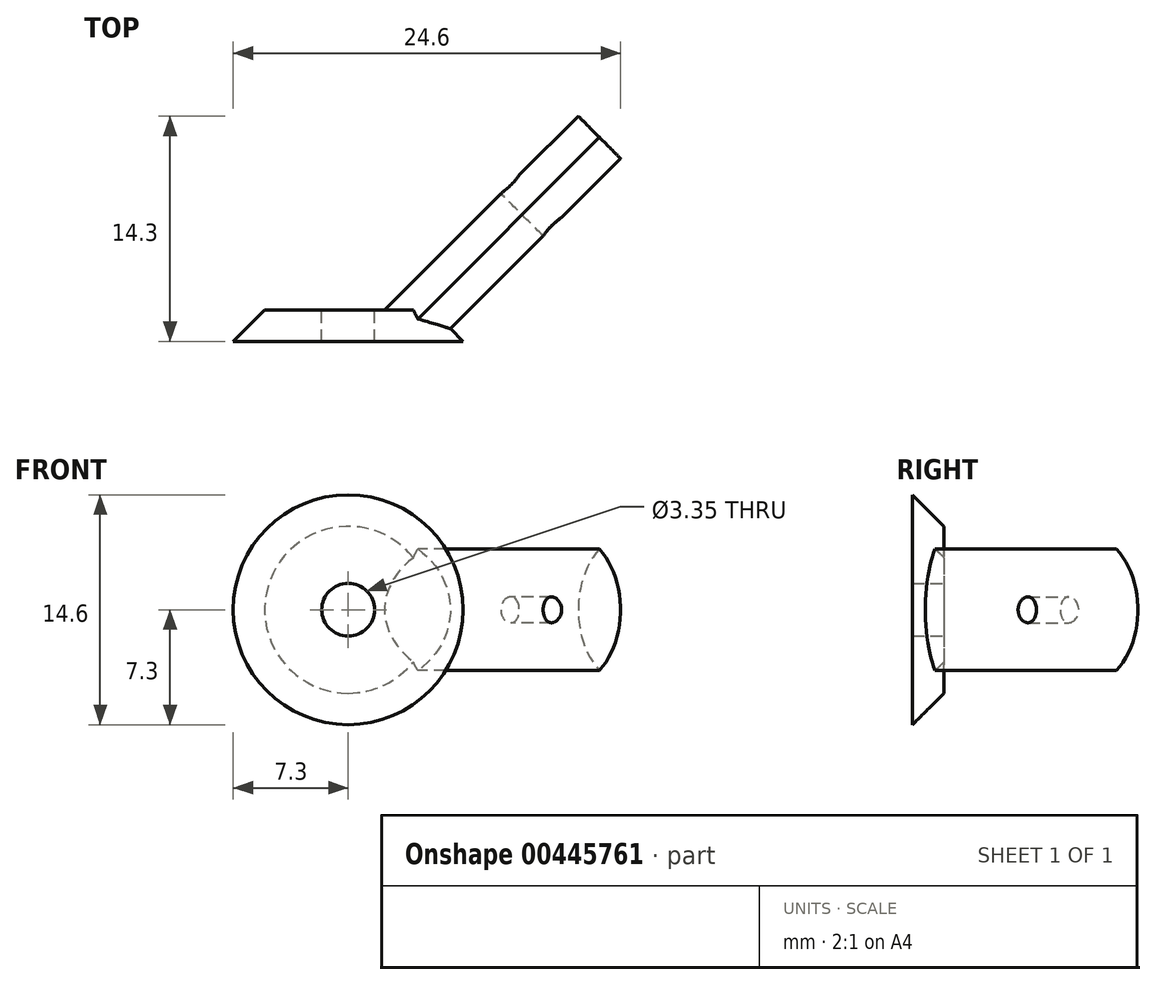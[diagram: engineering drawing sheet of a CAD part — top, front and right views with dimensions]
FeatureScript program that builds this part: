
annotation { "Feature Type Name" : "Feature", "Feature Type Description" : "" }
export const myFeature = defineFeature(function(context is Context, id is Id, definition is map)
    precondition{}
    {
        {
            var Q0;
            Q0=qCreatedBy(makeId("Front.planeOp"),FACE);
            var sketch = newSketch(context, id + "F0", { "sketchPlane" : qUnion([Q0])});
            skCircle(sketch, "E0", {"center": v(0, 0) * mm, "radius": 8.3 * mm});
            skSolve(sketch);
        }
        {
            var Q0;
            Q0=makeQuery(id+"F0.imprint","IMPRINT",FACE,{"disambiguationData":[TD([[makeQuery(id+"F0.imprint","IMPRINT",EDGE,{"derivedFrom":sQuery(id+"F0.wireOp",EDGE,"E0")}),1.0]])]});
            extrude(context, id + "F1", {"entities" : qUnion([Q0]), "depth" : 2 * mm});
        }
        {
            var Q0;
            Q0=makeQuery(id+"F1.opExtrude","CAP_FACE",FACE,{"disambiguationData":[OSD([sQuery(id+"F0.wireOp",EDGE,"E0")])],"isStart":true});
            var sketch = newSketch(context, id + "F2", { "sketchPlane" : qUnion([Q0])});
            skCircle(sketch, "E1", {"center": v(0, 0) * mm, "radius": 1.67 * mm});
            skSolve(sketch);
        }
        {
            var Q0;
            Q0=makeQuery(id+"F2.imprint","IMPRINT",FACE,{"disambiguationData":[TD([[makeQuery(id+"F2.imprint","IMPRINT",EDGE,{"derivedFrom":sQuery(id+"F2.wireOp",EDGE,"E1")}),1.0]])]});
            extrude(context, id + "F3", {"entities" : qUnion([Q0]), "operationType" : NewBodyOperationType.REMOVE, "oppositeDirection" : true, "depth" : 25 * mm});
        }
        {
            var Q0;
            Q0=qCreatedBy(makeId("Right.planeOp"),FACE);
            cPlane(context, id + "F4", {"entities" : qUnion([Q0]), "cplaneType" : CPlaneType.OFFSET, "offset" : 5 * mm, "width" : 150 * mm, "height" : 150 * mm});
        }
        {
            var Q0;
            Q0=qCreatedBy(id+"F4.planeOp",FACE);
            var sketch = newSketch(context, id + "F5", { "sketchPlane" : qUnion([Q0])});
            skLineSegment(sketch, "E2", {"start": v(0, 0) * mm, "end": v(0, 8.61) * mm, "construction": true});
            skSolve(sketch);
        }
        {
            var Q0;
            Q0=qCreatedBy(id+"F4.planeOp",FACE);
            var Q1;
            Q1=sQuery(id+"F5.wireOp",EDGE,"E2");
            cPlane(context, id + "F6", {"entities" : qUnion([Q0, Q1]), "cplaneType" : CPlaneType.LINE_ANGLE, "offset" : 0 * mm, "angle" : 45 * degree, "width" : 150 * mm, "height" : 150 * mm});
        }
        {
            var Q0;
            Q0=qCreatedBy(id+"F6.planeOp",FACE);
            var sketch = newSketch(context, id + "F7", { "sketchPlane" : qUnion([Q0])});
            skLineSegment(sketch, "E3", {"start": v(3.54, 3.85) * mm, "end": v(3.54, -3.85) * mm, "construction": true});
            skLineSegment(sketch, "E4", {"start": v(1.64, 0) * mm, "end": v(5.44, 0) * mm, "construction": true});
            skPoint(sketch, "E4.endSnap0", {"position": v(3.54, 0) * mm});
            skArc(sketch, "E5", {"start": v(3.54, -3.85) * mm, "mid": v(5.44, 0) * mm, "end": v(3.54, 3.85) * mm});
            skArc(sketch, "E6", {"start": v(3.54, 3.85) * mm, "mid": v(1.64, 0) * mm, "end": v(3.54, -3.85) * mm});
            skSolve(sketch);
        }
        {
            var Q0;
            Q0=makeQuery(id+"F7.imprint","IMPRINT",FACE,{"disambiguationData":[TD([[makeQuery(id+"F7.imprint","IMPRINT",EDGE,{"derivedFrom":sQuery(id+"F7.wireOp",EDGE,"E5")}),1.0]])]});
            var Q1;
            Q1=sQuery(id+"F7.wireOp",EDGE,"E6");
            var Q2;
            Q2=sQuery(id+"F7.wireOp",EDGE,"E5");
            var Q3;
            Q3=makeQuery(id+"F1.opExtrude","CAP_FACE",FACE,{"disambiguationData":[OSD([sQuery(id+"F0.wireOp",EDGE,"E0")])],"isStart":true});
            extrude(context, id + "F8", {"entities" : qUnion([Q0]), "operationType" : NewBodyOperationType.ADD, "surfaceEntities" : qUnion([Q1, Q2]), "oppositeDirection" : true, "depth" : 15.5 * mm, "hasSecondDirection" : true, "secondDirectionBound" : SecondDirectionBoundingType.UP_TO_SURFACE, "secondDirectionOppositeDirection" : false, "secondDirectionBoundEntityFace" : qUnion([Q3]), "secondDirectionDepth" : 25 * mm});
        }
        {
            var Q0;
            Q0=qCreatedBy(makeId("Top.planeOp"),FACE);
            var sketch = newSketch(context, id + "F9", { "sketchPlane" : qUnion([Q0])});
            skLineSegment(sketch, "E7", {"start": v(14.62, 12.3) * mm, "end": v(10.28, 7.97) * mm});
            skSolve(sketch);
        }
        {
            var Q0;
            Q0=makeQuery(id+"F8.opExtrude","SWEPT_FACE",FACE,{"disambiguationData":[OSD([sQuery(id+"F7.wireOp",EDGE,"E6")])]});
            var Q1;
            Q1=sQuery(id+"F9.wireOp",VERTEX,"E7.end");
            cPlane(context, id + "F10", {"entities" : qUnion([Q0, Q1]), "cplaneType" : CPlaneType.LINE_POINT, "offset" : 25 * mm, "width" : 150 * mm, "height" : 150 * mm});
        }
        {
            var Q0;
            Q0=qCreatedBy(id+"F10.planeOp",FACE);
            var sketch = newSketch(context, id + "F11", { "sketchPlane" : qUnion([Q0])});
            skLineSegment(sketch, "E8", {"start": v(1.6, 0) * mm, "end": v(1.6, -15.75) * mm, "construction": true});
            skSolve(sketch);
        }
        {
            var Q0;
            Q0=sQuery(id+"F11.wireOp",EDGE,"E8");
            var Q1;
            Q1=qCreatedBy(id+"F10.planeOp",FACE);
            cPlane(context, id + "F12", {"entities" : qUnion([Q0, Q1]), "cplaneType" : CPlaneType.LINE_ANGLE, "offset" : 25 * mm, "angle" : 90 * degree, "width" : 150 * mm, "height" : 150 * mm});
        }
        {
            var Q0;
            Q0=qCreatedBy(id+"F12.planeOp",FACE);
            var sketch = newSketch(context, id + "F13", { "sketchPlane" : qUnion([Q0])});
            skCircle(sketch, "E9", {"center": v(12.9, 0) * mm, "radius": 0.82 * mm});
            skSolve(sketch);
        }
        {
            var Q0;
            Q0=makeQuery(id+"F13.imprint","IMPRINT",FACE,{"disambiguationData":[TD([[makeQuery(id+"F13.imprint","IMPRINT",EDGE,{"derivedFrom":sQuery(id+"F13.wireOp",EDGE,"E9")}),1.0]])]});
            extrude(context, id + "F14", {"entities" : qUnion([Q0]), "operationType" : NewBodyOperationType.REMOVE, "depth" : 25 * mm});
        }
        {
            var Q0;
            Q0=makeQuery(id+"F1.opExtrude","CAP_EDGE",EDGE,{"disambiguationData":[OSD([sQuery(id+"F0.wireOp",EDGE,"E0")])],"isStart":true});
            chamfer(context, id + "F15", {"entities" : qUnion([Q0]), "width" : 3 * mm, "tangentPropagation" : true});
        }
    });
